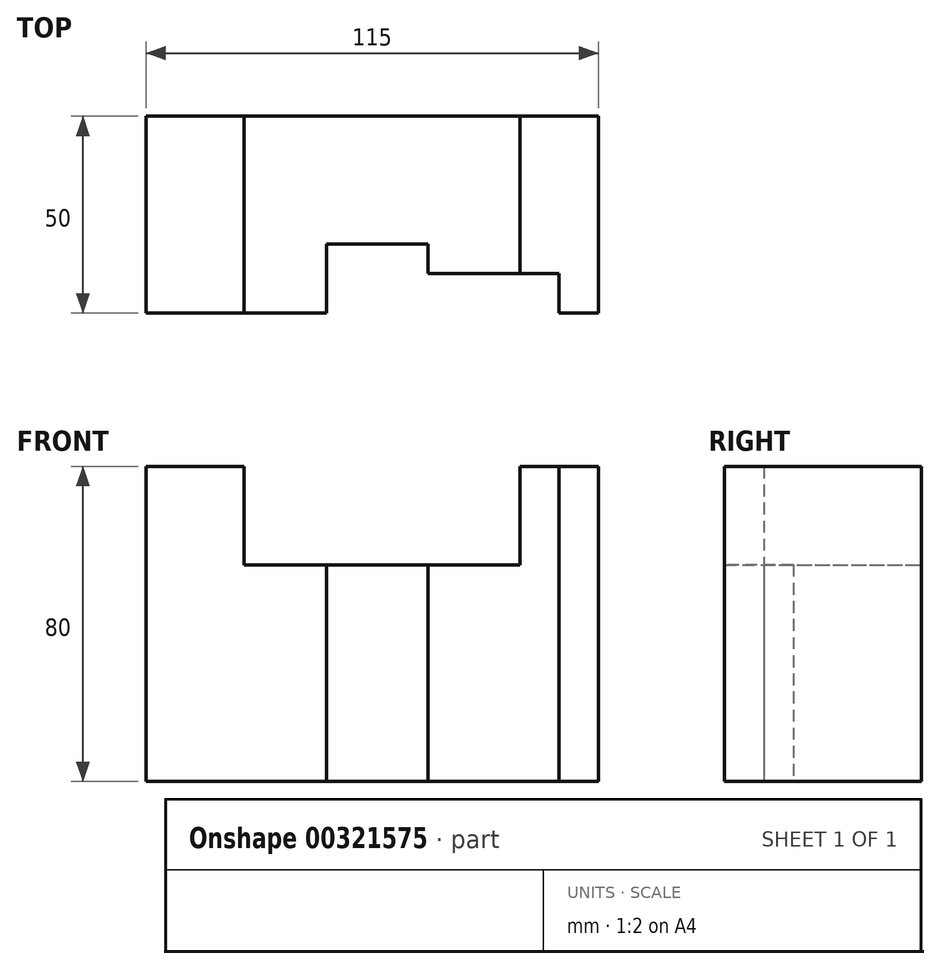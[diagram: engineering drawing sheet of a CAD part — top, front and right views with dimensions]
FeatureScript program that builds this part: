
annotation { "Feature Type Name" : "Feature", "Feature Type Description" : "" }
export const myFeature = defineFeature(function(context is Context, id is Id, definition is map)
    precondition{}
    {
        {
            var Q0;
            Q0=qCreatedBy(makeId("Front.planeOp"),FACE);
            var sketch = newSketch(context, id + "F0", { "sketchPlane" : qUnion([Q0])});
            skLineSegment(sketch, "E0", {"start": v(0, 80) * mm, "end": v(0, 0) * mm});
            skLineSegment(sketch, "E1", {"start": v(0, 0) * mm, "end": v(115, 0) * mm});
            skLineSegment(sketch, "E2", {"start": v(115, 0) * mm, "end": v(115, 80) * mm});
            skLineSegment(sketch, "E3", {"start": v(115, 80) * mm, "end": v(95, 80) * mm});
            skLineSegment(sketch, "E4", {"start": v(95, 80) * mm, "end": v(95, 55) * mm});
            skLineSegment(sketch, "E5", {"start": v(95, 55) * mm, "end": v(25, 55) * mm});
            skLineSegment(sketch, "E6", {"start": v(25, 55) * mm, "end": v(25, 80) * mm});
            skLineSegment(sketch, "E7", {"start": v(25, 80) * mm, "end": v(0, 80) * mm});
            skSolve(sketch);
        }
        {
            var Q0;
            Q0 = qSketchRegion(id + "F0", true);
            extrude(context, id + "F1", {"entities" : qUnion([Q0]), "depth" : 50 * mm});
        }
        {
            var Q0;
            Q0=makeQuery(id+"F1.opExtrude","CAP_FACE",FACE,{"disambiguationData":[OSD([sQuery(id+"F0.wireOp",EDGE,"E0"),sQuery(id+"F0.wireOp",EDGE,"E1"),sQuery(id+"F0.wireOp",EDGE,"E2"),sQuery(id+"F0.wireOp",EDGE,"E3"),sQuery(id+"F0.wireOp",EDGE,"E4"),sQuery(id+"F0.wireOp",EDGE,"E5"),sQuery(id+"F0.wireOp",EDGE,"E6"),sQuery(id+"F0.wireOp",EDGE,"E7")])],"isStart":false});
            var sketch = newSketch(context, id + "F2", { "sketchPlane" : qUnion([Q0])});
            skLineSegment(sketch, "E8.bottom", {"start": v(71.64, 55) * mm, "end": v(45.94, 55) * mm});
            skLineSegment(sketch, "E8.top", {"start": v(71.64, 0) * mm, "end": v(45.94, 0) * mm});
            skLineSegment(sketch, "E8.left", {"start": v(71.64, 55) * mm, "end": v(71.64, 0) * mm});
            skLineSegment(sketch, "E8.right", {"start": v(45.94, 55) * mm, "end": v(45.94, 0) * mm});
            skLineSegment(sketch, "E9", {"start": v(105, 80) * mm, "end": v(105, 0) * mm});
            skSolve(sketch);
        }
        {
            var Q0;
            Q0=makeQuery(id+"F2.imprint","IMPRINT",FACE,{"disambiguationData":[TD([[makeQuery(id+"F2.imprint","IMPRINT",EDGE,{"derivedFrom":sQuery(id+"F2.wireOp",EDGE,"E8.bottom")}),1.0]])]});
            extrude(context, id + "F3", {"entities" : qUnion([Q0]), "operationType" : NewBodyOperationType.REMOVE, "endBound" : BoundingType.SYMMETRIC, "oppositeDirection" : true, "depth" : 35 * mm});
        }
        {
            var Q0;
            {var subQ3=sQuery(id+"F2.wireOp",EDGE,"E8.left");Q0=makeQuery(id+"F2.imprint","IMPRINT",FACE,{"disambiguationData":[TD([[makeQuery(id+"F2.imprint","IMPRINT",EDGE,{"derivedFrom":subQ3}),1.0]])]});}
            extrude(context, id + "F4", {"entities" : qUnion([Q0]), "operationType" : NewBodyOperationType.REMOVE, "oppositeDirection" : true, "depth" : 10 * mm});
        }
    });
